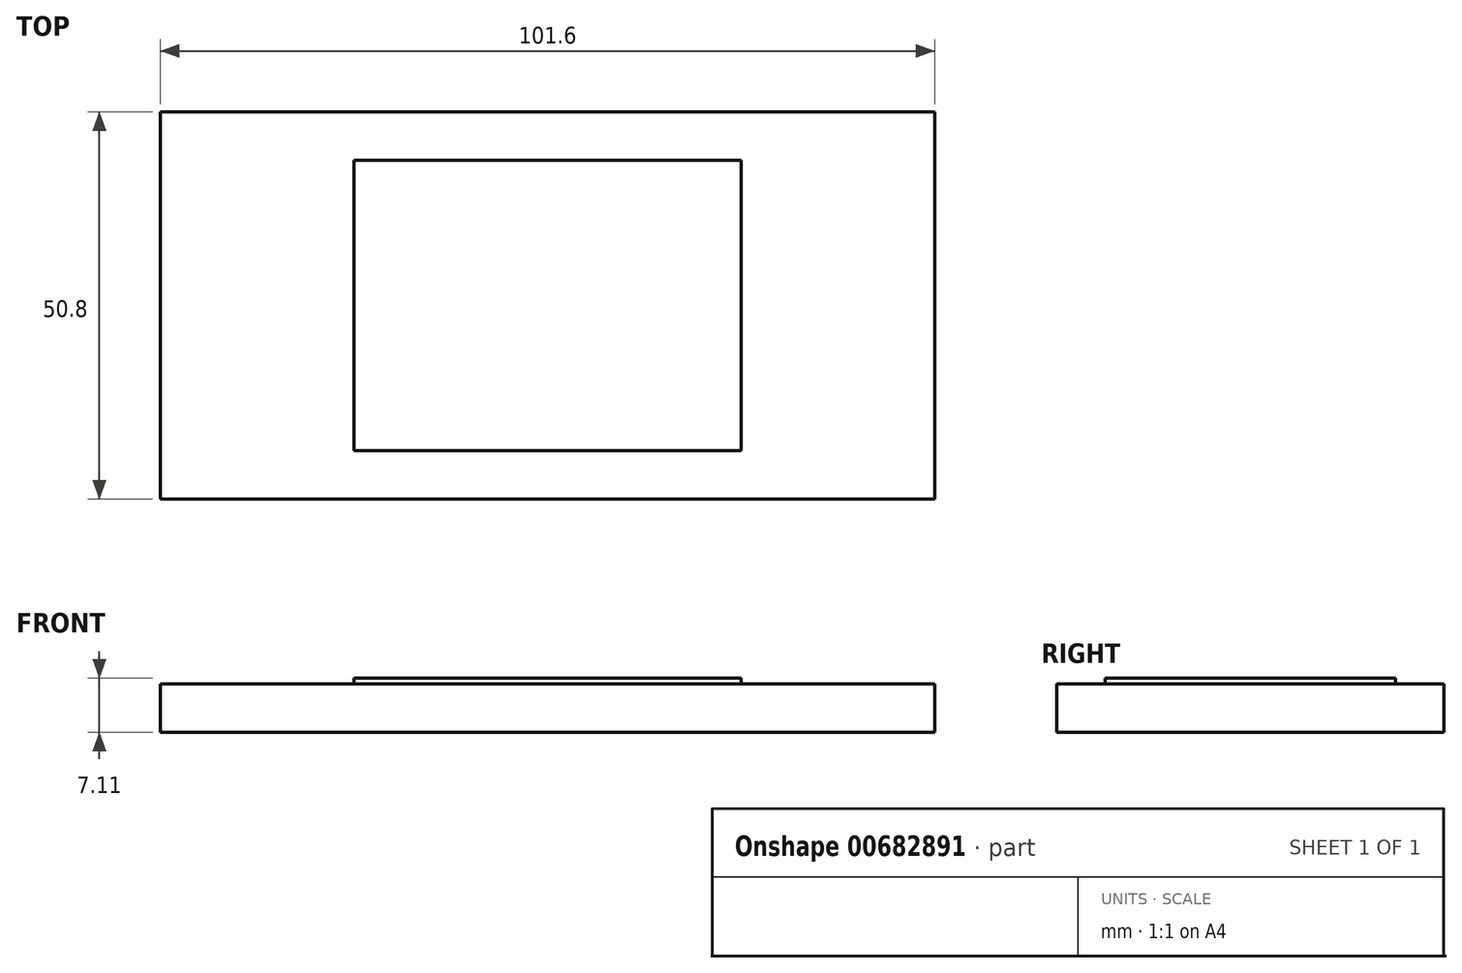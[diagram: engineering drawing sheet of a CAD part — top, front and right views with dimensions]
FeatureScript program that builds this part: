
annotation { "Feature Type Name" : "Feature", "Feature Type Description" : "" }
export const myFeature = defineFeature(function(context is Context, id is Id, definition is map)
    precondition{}
    {
        {
            var Q0;
            Q0=qCreatedBy(makeId("Top.planeOp"),FACE);
            var sketch = newSketch(context, id + "F0", { "sketchPlane" : qUnion([Q0])});
            skLineSegment(sketch, "E0.bottom", {"start": v(-50.8, 25.4) * mm, "end": v(50.8, 25.4) * mm});
            skLineSegment(sketch, "E0.top", {"start": v(-50.8, -25.4) * mm, "end": v(50.8, -25.4) * mm});
            skLineSegment(sketch, "E0.left", {"start": v(-50.8, 25.4) * mm, "end": v(-50.8, -25.4) * mm});
            skLineSegment(sketch, "E0.right", {"start": v(50.8, 25.4) * mm, "end": v(50.8, -25.4) * mm});
            skPoint(sketch, "E0.middle", {"position": v(0, 0) * mm});
            skSolve(sketch);
        }
        {
            var Q0;
            Q0 = qSketchRegion(id + "F0", true);
            var Q1;
            Q1=makeQuery(id+"F0.imprint","IMPRINT",FACE,{"disambiguationData":[TD([[makeQuery(id+"F0.imprint","IMPRINT",EDGE,{"derivedFrom":sQuery(id+"F0.wireOp",EDGE,"E0.bottom")}),-1.0]])]});
            extrude(context, id + "F1", {"entities" : qUnion([Q0, Q1]), "depth" : 6.35 * mm, "offsetDistance" : 25.4 * mm});
        }
        {
            var Q0;
            Q0=makeQuery(id+"F1.opExtrude","CAP_FACE",FACE,{"disambiguationData":[OSD([sQuery(id+"F0.wireOp",EDGE,"E0.bottom"),sQuery(id+"F0.wireOp",EDGE,"E0.top"),sQuery(id+"F0.wireOp",EDGE,"E0.left"),sQuery(id+"F0.wireOp",EDGE,"E0.right")])],"isStart":false});
            var sketch = newSketch(context, id + "F2", { "sketchPlane" : qUnion([Q0])});
            skLineSegment(sketch, "E1.bottom", {"start": v(-25.4, 19.05) * mm, "end": v(25.4, 19.05) * mm});
            skLineSegment(sketch, "E1.top", {"start": v(-25.4, -19.05) * mm, "end": v(25.4, -19.05) * mm});
            skLineSegment(sketch, "E1.left", {"start": v(-25.4, 19.05) * mm, "end": v(-25.4, -19.05) * mm});
            skLineSegment(sketch, "E1.right", {"start": v(25.4, 19.05) * mm, "end": v(25.4, -19.05) * mm});
            skPoint(sketch, "E1.middle", {"position": v(0, 0) * mm});
            skSolve(sketch);
        }
        {
            var Q0;
            Q0=makeQuery(id+"F2.imprint","IMPRINT",FACE,{"disambiguationData":[TD([[makeQuery(id+"F2.imprint","IMPRINT",EDGE,{"derivedFrom":sQuery(id+"F2.wireOp",EDGE,"E1.bottom")}),-1.0]])]});
            extrude(context, id + "F3", {"entities" : qUnion([Q0]), "operationType" : NewBodyOperationType.ADD, "depth" : 0.76 * mm, "offsetDistance" : 25.4 * mm});
        }
    });
